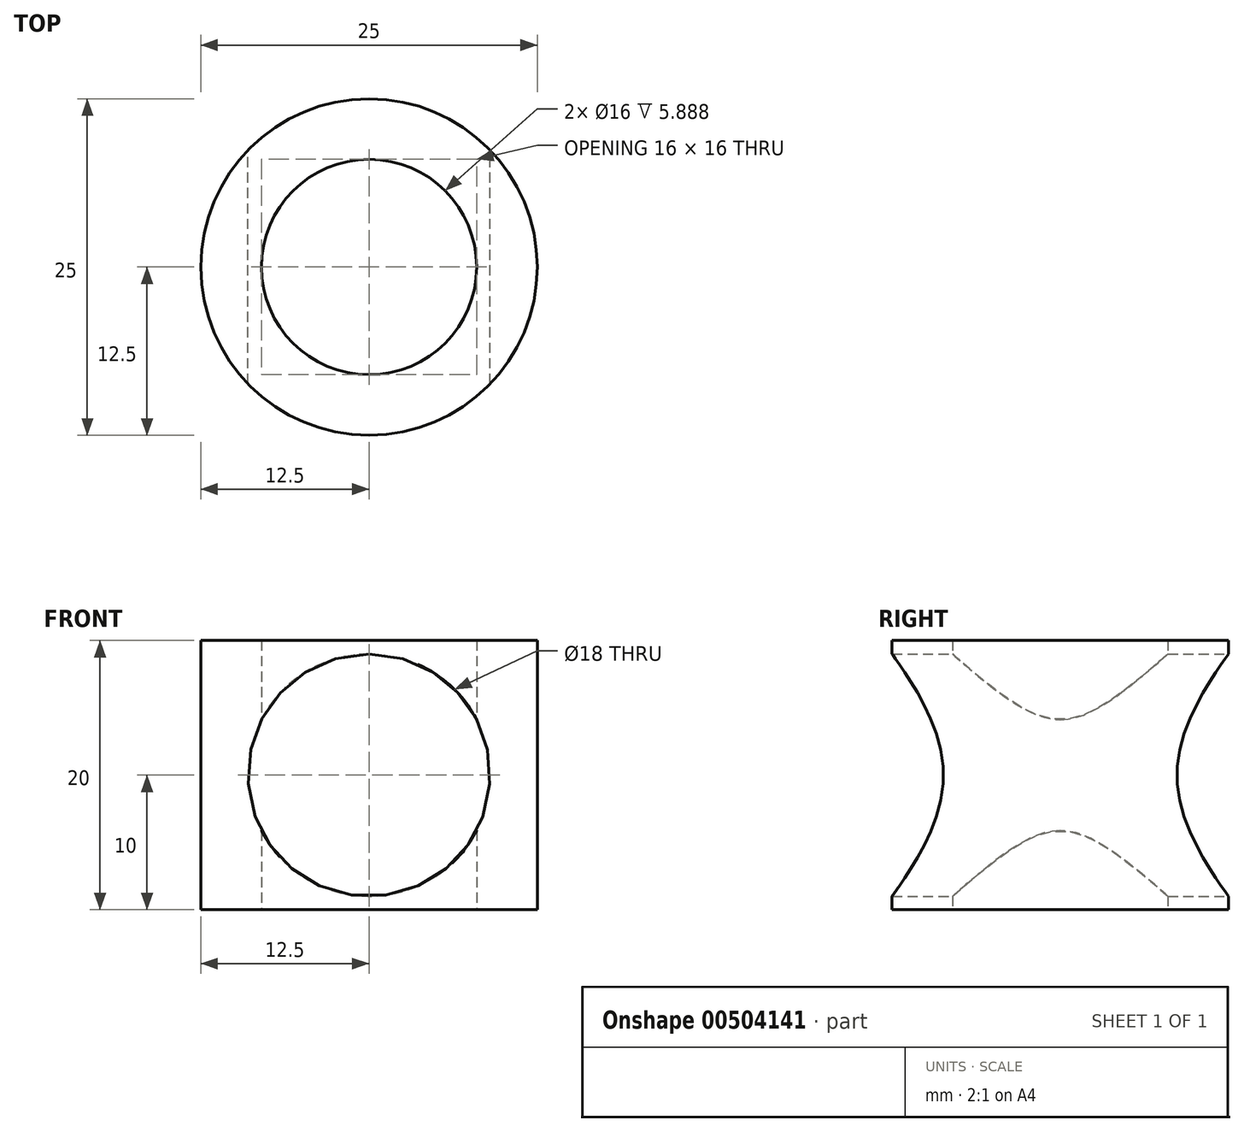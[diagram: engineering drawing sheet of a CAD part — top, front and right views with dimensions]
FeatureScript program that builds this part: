
annotation { "Feature Type Name" : "Feature", "Feature Type Description" : "" }
export const myFeature = defineFeature(function(context is Context, id is Id, definition is map)
    precondition{}
    {
        {
            var Q0;
            Q0=qCreatedBy(makeId("Top.planeOp"),FACE);
            var sketch = newSketch(context, id + "F0", { "sketchPlane" : qUnion([Q0])});
            skCircle(sketch, "E0", {"center": v(0, 0) * mm, "radius": 12.5 * mm});
            skCircle(sketch, "E1", {"center": v(0, 0) * mm, "radius": 8 * mm});
            skSolve(sketch);
        }
        {
            var Q0;
            Q0 = qSketchRegion(id + "F0", true);
            extrude(context, id + "F1", {"entities" : qUnion([Q0]), "depth" : 20 * mm, "offsetDistance" : 25 * mm});
        }
        {
            var Q0;
            Q0=qCreatedBy(makeId("Front.planeOp"),FACE);
            var sketch = newSketch(context, id + "F2", { "sketchPlane" : qUnion([Q0])});
            skCircle(sketch, "E2", {"center": v(0, 10) * mm, "radius": 9 * mm});
            skSolve(sketch);
        }
        {
            var Q0;
            Q0 = qSketchRegion(id + "F2", true);
            extrude(context, id + "F3", {"entities" : qUnion([Q0]), "operationType" : NewBodyOperationType.REMOVE, "endBound" : BoundingType.SYMMETRIC, "depth" : 25 * mm, "offsetDistance" : 25 * mm});
        }
    });
